# Revit family: P210876JX-042_JMW2427LL
name_source: partatom
category: Specialty Equipment
units: mm (PartAtom-declared; Revit-internal decimal feet)

## family parameters
Always vertical = Yes
Cut with Voids When Loaded = No
Enable Cutting in Views = No
Maintain Annotation Orientation = No
Part Type = Normal
Room Calculation Point = No
Round Connector Dimension = Use Diameter
Shared = No
Work Plane-Based = No

## types (1)
- JMW2427LL
    Accent Material = ARCAT - Metal - Steel - Stainless
    Apparent Load = 0 VA
    Body Material = ARCAT - Metal - Steel - Stainless
    Clearance Material = ARCAT - Clearance
    Default Elevation = 0"
    Depth = 23 1/4"
    Display Panel Material = ARCAT - Glass - Black
    Door Front Panel Material = ARCAT - Metal - Steel - Stainless
    Door Material = ARCAT - Metal - Steel - Stainless
    Glass Material = ARCAT - Glass - Tempered - Black
    Handle Material = ARCAT - Metal - Steel - Grey
    Height = 43 3/4"
    Manufacturer = JennAir
    Model = JMW2427LL
    Voltage = 0 V
    Width = 27"

## geometry (parser evidence)
native form markers: Sweep x3
no freeform markers — native parametric forms only
